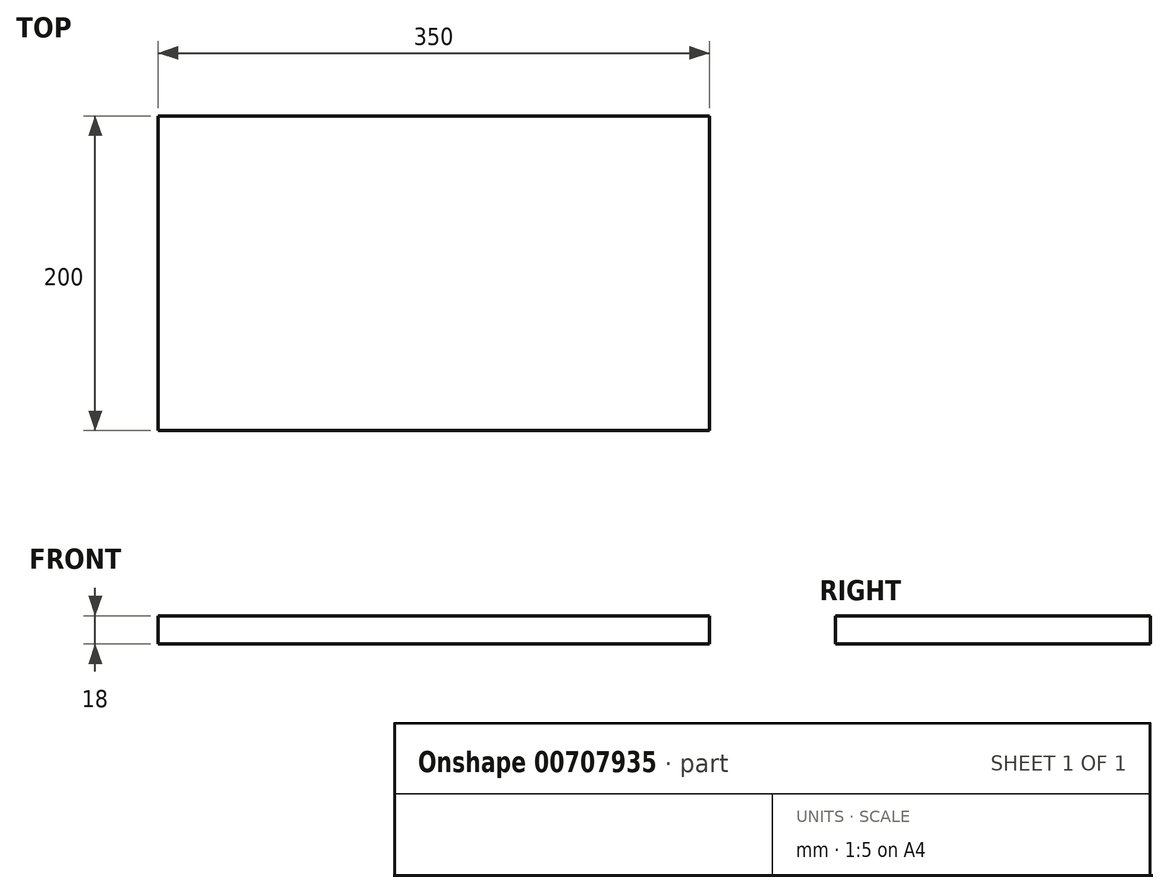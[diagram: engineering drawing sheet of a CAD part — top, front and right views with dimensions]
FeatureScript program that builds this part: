
annotation { "Feature Type Name" : "Feature", "Feature Type Description" : "" }
export const myFeature = defineFeature(function(context is Context, id is Id, definition is map)
    precondition{}
    {
        {
            var Q0;
            Q0=qCreatedBy(makeId("Top.planeOp"),FACE);
            var sketch = newSketch(context, id + "F0", { "sketchPlane" : qUnion([Q0])});
            skLineSegment(sketch, "E0.bottom", {"start": v(0, 0) * mm, "end": v(350, 0) * mm});
            skLineSegment(sketch, "E0.top", {"start": v(0, 200) * mm, "end": v(350, 200) * mm});
            skLineSegment(sketch, "E0.left", {"start": v(0, 0) * mm, "end": v(0, 200) * mm});
            skLineSegment(sketch, "E0.right", {"start": v(350, 0) * mm, "end": v(350, 200) * mm});
            skLineSegment(sketch, "E1", {"start": v(175, 200) * mm, "end": v(175, 0) * mm, "construction": true});
            skLineSegment(sketch, "E2.bottom", {"start": v(-18, 0) * mm, "end": v(368, 0) * mm});
            skLineSegment(sketch, "E2.top", {"start": v(-18, -4) * mm, "end": v(368, -4) * mm});
            skLineSegment(sketch, "E2.left", {"start": v(-18, 0) * mm, "end": v(-18, -4) * mm});
            skLineSegment(sketch, "E2.right", {"start": v(368, 0) * mm, "end": v(368, -4) * mm});
            skLineSegment(sketch, "E3.bottom", {"start": v(-18, 204) * mm, "end": v(368, 204) * mm});
            skLineSegment(sketch, "E3.top", {"start": v(-18, 200) * mm, "end": v(368, 200) * mm});
            skLineSegment(sketch, "E3.left", {"start": v(-18, 204) * mm, "end": v(-18, 200) * mm});
            skLineSegment(sketch, "E3.right", {"start": v(368, 204) * mm, "end": v(368, 200) * mm});
            skSolve(sketch);
        }
        {
            var Q0;
            {var subQ0=sQuery(id+"F0.wireOp",EDGE,"E0.left");Q0=makeQuery(id+"F0.imprint","IMPRINT",FACE,{"disambiguationData":[TD([[makeQuery(id+"F0.imprint","IMPRINT",EDGE,{"derivedFrom":subQ0}),-1.0]])]});}
            extrude(context, id + "F1", {"entities" : qUnion([Q0]), "depth" : 18 * mm, "offsetDistance" : 25 * mm});
        }
    });
